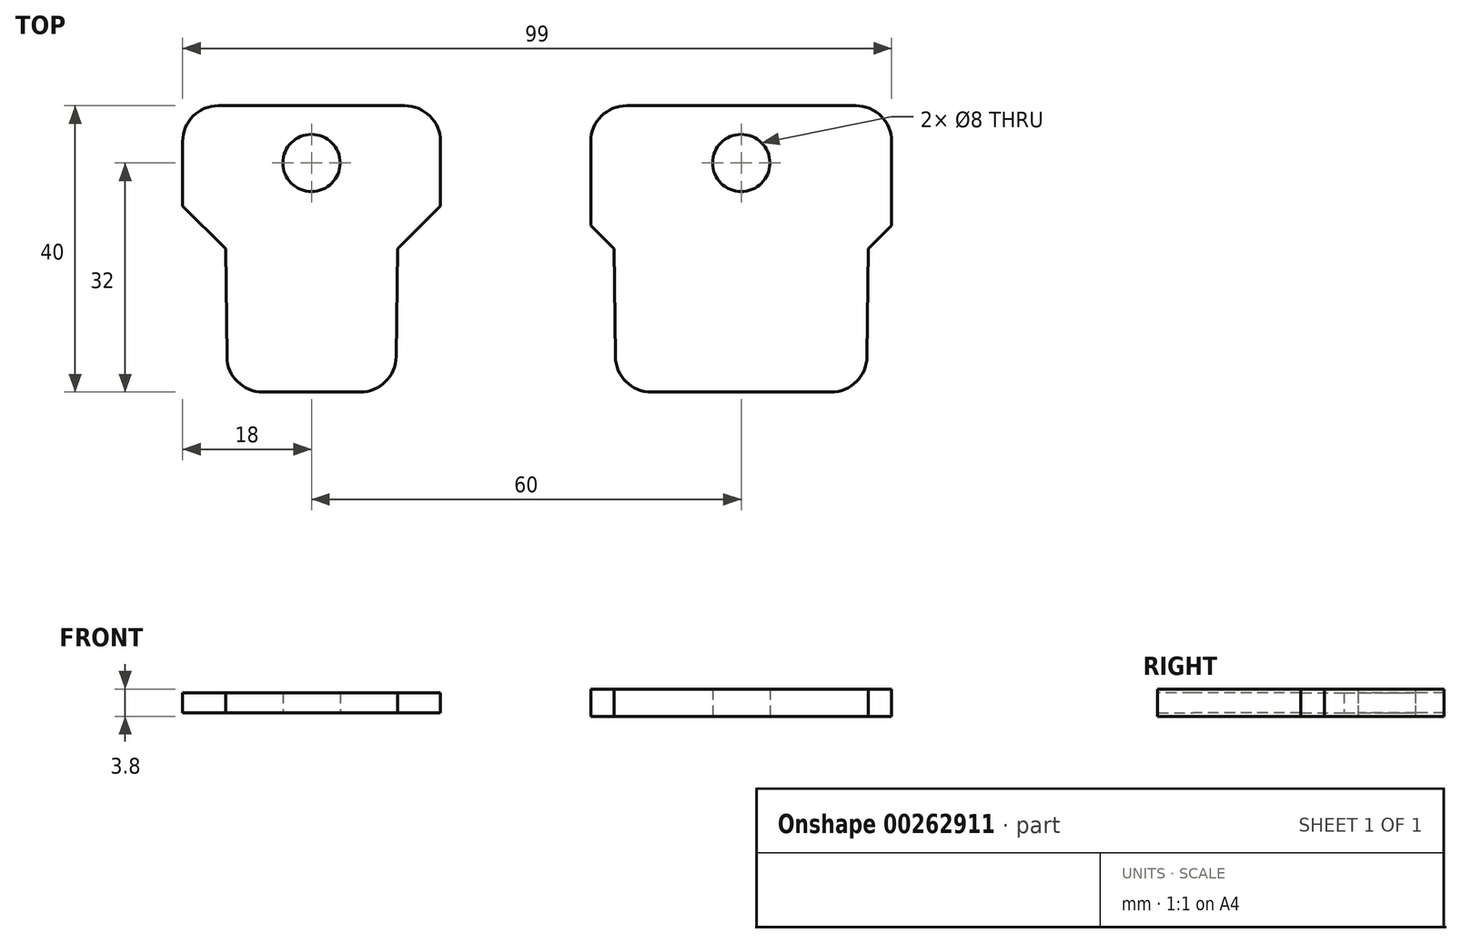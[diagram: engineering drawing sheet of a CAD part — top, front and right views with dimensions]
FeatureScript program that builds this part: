
annotation { "Feature Type Name" : "Feature", "Feature Type Description" : "" }
export const myFeature = defineFeature(function(context is Context, id is Id, definition is map)
    precondition{}
    {
        {
            var Q0;
            Q0=qCreatedBy(makeId("Top.planeOp"),FACE);
            var sketch = newSketch(context, id + "F0", { "sketchPlane" : qUnion([Q0])});
            skLineSegment(sketch, "E0.top", {"start": v(-17.5, -20) * mm, "end": v(17.5, -20) * mm});
            skLineSegment(sketch, "E0.left", {"start": v(-17.75, 0) * mm, "end": v(-17.5, -20) * mm});
            skLineSegment(sketch, "E1.top", {"start": v(-21, 20) * mm, "end": v(21, 20) * mm});
            skLineSegment(sketch, "E1.left", {"start": v(-21, 3.25) * mm, "end": v(-21, 20) * mm});
            skLineSegment(sketch, "E1.right", {"start": v(21, 3.25) * mm, "end": v(21, 20) * mm});
            skPoint(sketch, "E2", {"position": v(0, 20) * mm});
            skPoint(sketch, "E3", {"position": v(0, -20) * mm});
            skLineSegment(sketch, "E4", {"start": v(-17.75, 0) * mm, "end": v(-21, 3.25) * mm});
            skLineSegment(sketch, "E5", {"start": v(17.75, 0) * mm, "end": v(21, 3.25) * mm});
            skLineSegment(sketch, "E6", {"start": v(-17.75, 0) * mm, "end": v(17.75, 0) * mm, "construction": true});
            skPoint(sketch, "E7", {"position": v(0, 0) * mm});
            skLineSegment(sketch, "E8", {"start": v(17.5, -20) * mm, "end": v(17.75, 0) * mm});
            skCircle(sketch, "E9", {"center": v(0, 12) * mm, "radius": 4 * mm});
            skSolve(sketch);
        }
        {
            var Q0;
            Q0 = qSketchRegion(id + "F0", true);
            extrude(context, id + "F1", {"entities" : qUnion([Q0]), "depth" : 3.8 * mm, "symmetric" : true});
        }
        {
            var Q0;
            Q0=qCreatedBy(makeId("Top.planeOp"),FACE);
            var sketch = newSketch(context, id + "F2", { "sketchPlane" : qUnion([Q0])});
            skLineSegment(sketch, "E10.top", {"start": v(-71.75, -20) * mm, "end": v(-48.25, -20) * mm});
            skLineSegment(sketch, "E10.left", {"start": v(-72, 0) * mm, "end": v(-71.75, -20) * mm});
            skLineSegment(sketch, "E11.top", {"start": v(-78, 20) * mm, "end": v(-42, 20) * mm});
            skLineSegment(sketch, "E11.left", {"start": v(-78, 6) * mm, "end": v(-78, 20) * mm});
            skLineSegment(sketch, "E11.right", {"start": v(-42, 6) * mm, "end": v(-42, 20) * mm});
            skPoint(sketch, "E12", {"position": v(-60, 20) * mm});
            skPoint(sketch, "E13", {"position": v(-60, -20) * mm});
            skLineSegment(sketch, "E14", {"start": v(-72, 0) * mm, "end": v(-78, 6) * mm});
            skLineSegment(sketch, "E15", {"start": v(-48, 0) * mm, "end": v(-42, 6) * mm});
            skLineSegment(sketch, "E16", {"start": v(-72, 0) * mm, "end": v(-48, 0) * mm, "construction": true});
            skPoint(sketch, "E17", {"position": v(-60, 0) * mm});
            skLineSegment(sketch, "E18", {"start": v(-48.25, -20) * mm, "end": v(-48, 0) * mm});
            skCircle(sketch, "E19", {"center": v(-60, 12) * mm, "radius": 4 * mm});
            skSolve(sketch);
        }
        {
            var Q0;
            Q0 = qSketchRegion(id + "F2", true);
            extrude(context, id + "F3", {"entities" : qUnion([Q0]), "depth" : 2.8 * mm, "symmetric" : true});
        }
        {
            var Q0;
            Q0=makeQuery(id+"F1.opExtrude","SWEPT_EDGE",EDGE,{"disambiguationData":[OSD([sQuery(id+"F0.wireOp",EDGE,"E1.top"),sQuery(id+"F0.wireOp",EDGE,"E1.left")])]});
            var Q1;
            Q1=makeQuery(id+"F1.opExtrude","SWEPT_EDGE",EDGE,{"disambiguationData":[OSD([sQuery(id+"F0.wireOp",EDGE,"E1.top"),sQuery(id+"F0.wireOp",EDGE,"E1.right")])]});
            var Q2;
            Q2=makeQuery(id+"F1.opExtrude","SWEPT_EDGE",EDGE,{"disambiguationData":[OSD([sQuery(id+"F0.wireOp",EDGE,"E0.top"),sQuery(id+"F0.wireOp",EDGE,"E8")])]});
            var Q3;
            Q3=makeQuery(id+"F1.opExtrude","SWEPT_EDGE",EDGE,{"disambiguationData":[OSD([sQuery(id+"F0.wireOp",EDGE,"E0.top"),sQuery(id+"F0.wireOp",EDGE,"E0.left")])]});
            var Q4;
            Q4=makeQuery(id+"F3.opExtrude","SWEPT_EDGE",EDGE,{"disambiguationData":[OSD([sQuery(id+"F2.wireOp",EDGE,"E10.top"),sQuery(id+"F2.wireOp",EDGE,"E10.left")])]});
            var Q5;
            Q5=makeQuery(id+"F3.opExtrude","SWEPT_EDGE",EDGE,{"disambiguationData":[OSD([sQuery(id+"F2.wireOp",EDGE,"E10.top"),sQuery(id+"F2.wireOp",EDGE,"E18")])]});
            var Q6;
            Q6=makeQuery(id+"F3.opExtrude","SWEPT_EDGE",EDGE,{"disambiguationData":[OSD([sQuery(id+"F2.wireOp",EDGE,"E11.top"),sQuery(id+"F2.wireOp",EDGE,"E11.right")])]});
            var Q7;
            Q7=makeQuery(id+"F3.opExtrude","SWEPT_EDGE",EDGE,{"disambiguationData":[OSD([sQuery(id+"F2.wireOp",EDGE,"E11.top"),sQuery(id+"F2.wireOp",EDGE,"E11.left")])]});
            fillet(context, id + "F4", {"entities" : qUnion([Q0, Q1, Q2, Q3, Q4, Q5, Q6, Q7]), "radius" : 5 * mm, "tangentPropagation" : true, "allowEdgeOverflow" : false});
        }
    });
